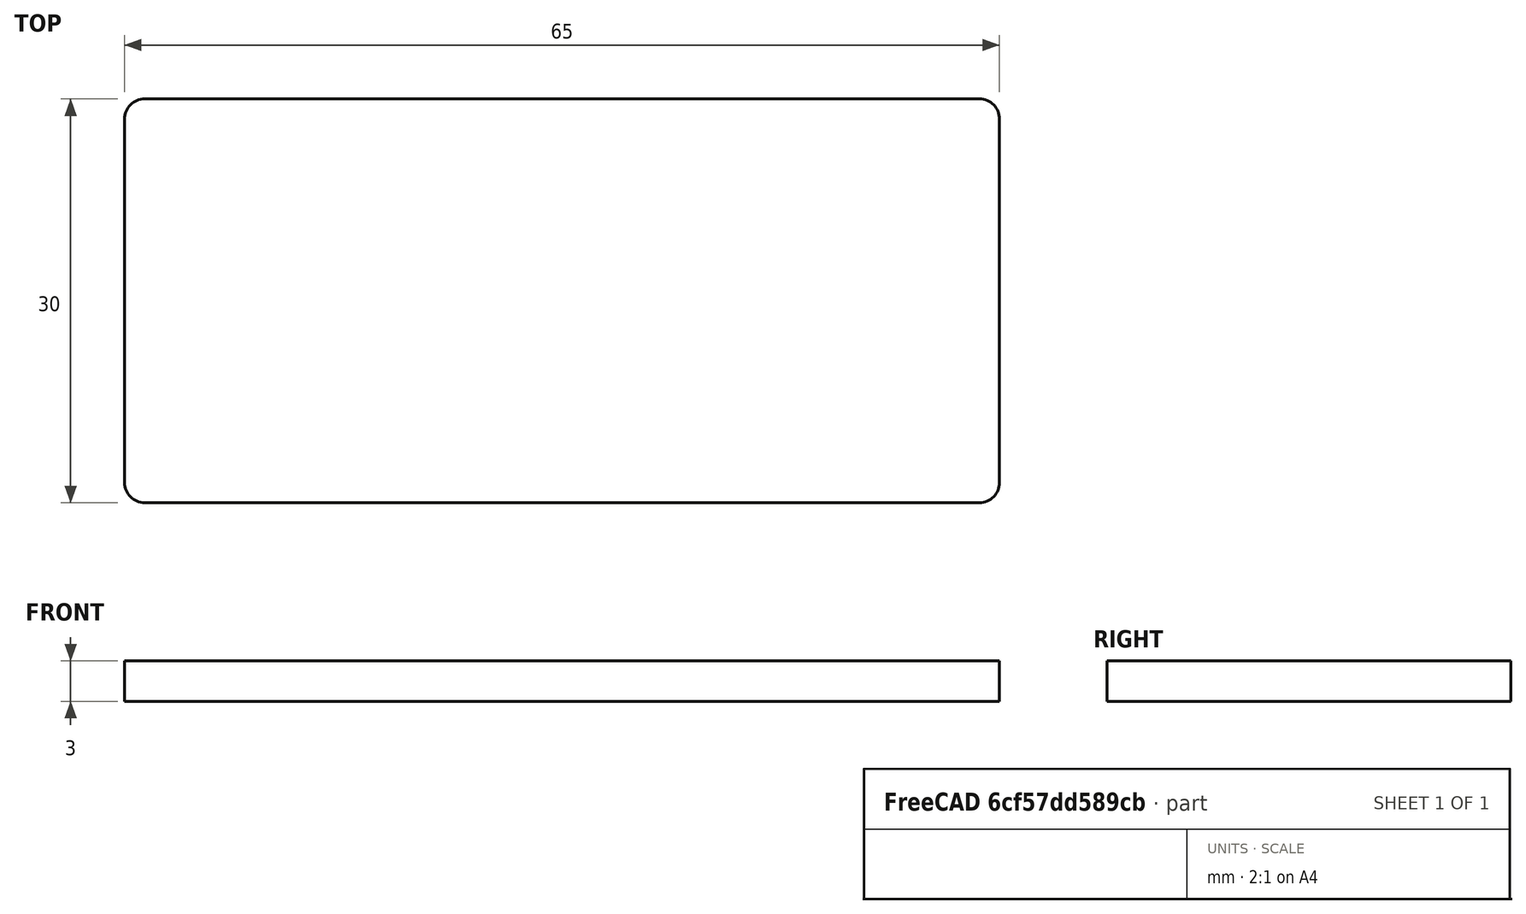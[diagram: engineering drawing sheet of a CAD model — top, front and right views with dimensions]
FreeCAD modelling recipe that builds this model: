
FCSTD DOCUMENT  (FreeCAD 0.19R)
Label: pca9685
License: All rights reserved
LicenseURL: http://en.wikipedia.org/wiki/All_rights_reserved
objects: Sketcher::SketchObject×1, PartDesign::Pad×1, PartDesign::Body×1
note: 4 computed .brp shape members not serialized (recipe doc carries the construction recipe); baked Part::Feature solids carry a one-line shape summary decoded from their .brp

FEATURE [Sketcher::SketchObject] Sketch
  MapMode = 5
  Support = -> [XY_Plane]
  sketch-geometry (8):
    g0: LineSegment StartX=-5.7e-14 StartY=30 StartZ=0 EndX=62 EndY=30 EndZ=0
    g1: LineSegment StartX=63.5 StartY=28.5 StartZ=0 EndX=63.5 EndY=1.5 EndZ=0
    g2: LineSegment StartX=62 StartY=0 StartZ=0 EndX=0 EndY=0 EndZ=0
    g3: LineSegment StartX=-1.5 StartY=1.5 StartZ=0 EndX=-1.5 EndY=28.5 EndZ=0
    g4: ArcOfCircle CenterX=-5.69e-14 CenterY=1.5 CenterZ=0 NormalX=0 NormalY=0 NormalZ=1 AngleXU=0 Radius=1.5 StartAngle=3.14159 EndAngle=4.71239
    g5: ArcOfCircle CenterX=-5.71e-14 CenterY=28.5 CenterZ=0 NormalX=0 NormalY=0 NormalZ=1 AngleXU=0 Radius=1.5 StartAngle=1.5708 EndAngle=3.14159
    g6: ArcOfCircle CenterX=62 CenterY=28.5 CenterZ=0 NormalX=0 NormalY=0 NormalZ=1 AngleXU=0 Radius=1.5 StartAngle=-9e-16 EndAngle=1.5708
    g7: ArcOfCircle CenterX=62 CenterY=1.5 CenterZ=0 NormalX=0 NormalY=0 NormalZ=1 AngleXU=0 Radius=1.5 StartAngle=4.71239 EndAngle=6.28319
  constraints (19):
    c: Horizontal(g0)
    c: Horizontal(g2)
    c: Vertical(g1)
    c: Vertical(g3)
    c: Tangent(g2,g4) = 1.5708
    c: Tangent(g3,g4) = 1.5708
    c: Tangent(g0,g5) = 1.5708
    c: Tangent(g3,g5) = 1.5708
    c: Tangent(g0,g6) = 1.5708
    c: Tangent(g1,g6) = 1.5708
    c: Tangent(g1,g7) = 1.5708
    c: Tangent(g2,g7) = 1.5708
    c: Equal(g7,g6)
    c: Equal(g6,g5)
    c: Equal(g5,g4)
    c: Radius(g5) = 1.5
    c: Distance(g3,g1) = 65
    c: Distance(g2,g0) = 30
    c: Coincident(g2,g-1)
FEATURE [PartDesign::Pad] Pad
  Length = 3
  Length2 = 100
  Profile = -> Sketch
  Type = 0
FEATURE [PartDesign::Body] Body
  Group = -> [Sketch,Pad]
  Origin = -> Origin
  Tip = -> Pad
